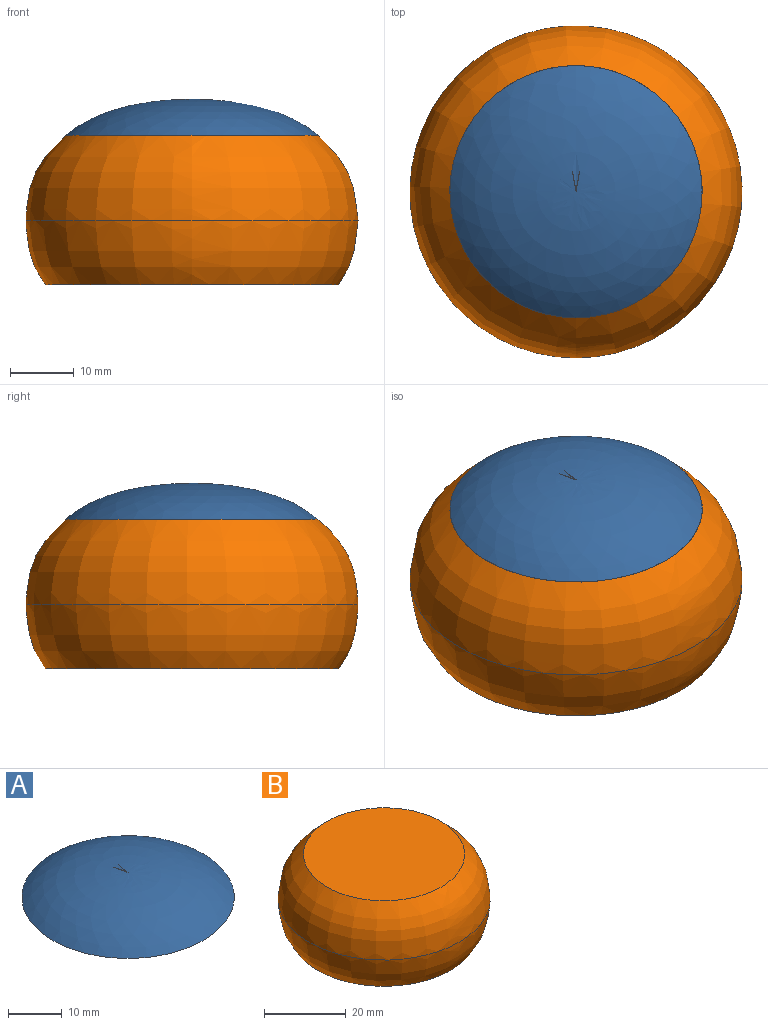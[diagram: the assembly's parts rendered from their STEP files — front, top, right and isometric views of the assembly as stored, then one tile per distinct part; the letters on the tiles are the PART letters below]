
ASSEMBLY  parts=2 mates=1
PART A: 2 faces, bbox 39.5x39.5x5.6 mm
  f0: revolved ~39.5x39.5mm, area 1347.7mm2, adj f1
  f1: plane 39.5x39.5mm, normal (0,0,-1), area 1225.4mm2, adj f0
PART B: 4 faces, bbox 52x52x23.4 mm
  f0: plane 39.5x39.5mm, normal (0,0,1), area 1225.4mm2, adj f1
  f1: revolved ~52x52mm, area 2305.7mm2, adj f0
  f2: revolved ~52x52mm, area 3350.4mm2, adj f3
  f3: plane 45.95x45.95mm, normal (0,0,-1), area 1658.6mm2, adj f2
PLACE A t=(-0.16,13.59,32.52)mm
PLACE B t=(-0.16,13.59,32.52)mm
MATE fastened B.f0 <-> A.f1  axis (0,0,1) through (-0.16,13.59,45.9)mm
